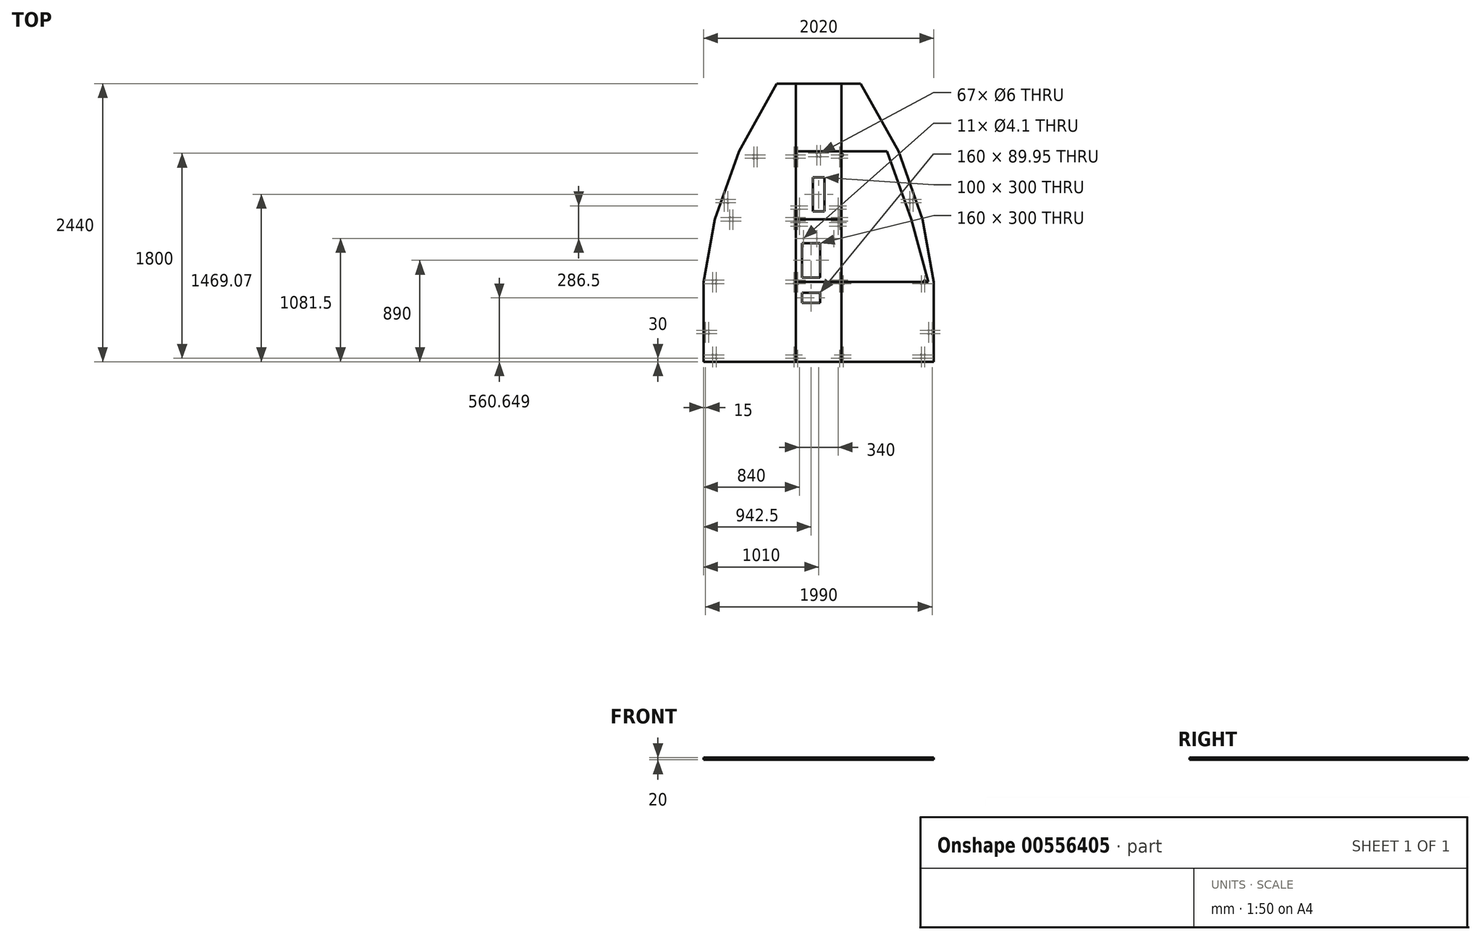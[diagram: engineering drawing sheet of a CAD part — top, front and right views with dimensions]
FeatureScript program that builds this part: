
annotation { "Feature Type Name" : "Feature", "Feature Type Description" : "" }
export const myFeature = defineFeature(function(context is Context, id is Id, definition is map)
    precondition{}
    {
        {
            var Q0;
            Q0=qCreatedBy(makeId("Top.planeOp"),FACE);
            var sketch = newSketch(context, id + "F0", { "sketchPlane" : qUnion([Q0])});
            skLineSegment(sketch, "E0.bottom", {"start": v(200, -350) * mm, "end": v(-200, -350) * mm});
            skLineSegment(sketch, "E0.top", {"start": v(200, 350) * mm, "end": v(-200, 350) * mm});
            skLineSegment(sketch, "E0.left", {"start": v(200, -350) * mm, "end": v(200, 350) * mm});
            skLineSegment(sketch, "E0.right", {"start": v(-200, -350) * mm, "end": v(-200, 350) * mm});
            skPoint(sketch, "E0.middle", {"position": v(0, 0) * mm});
            skCircle(sketch, "E1", {"center": v(185, 335) * mm, "radius": 3 * mm});
            skCircle(sketch, "E2", {"center": v(-185, 335) * mm, "radius": 3 * mm});
            skCircle(sketch, "E3", {"center": v(185, -320) * mm, "radius": 3 * mm});
            skCircle(sketch, "E4", {"center": v(-185, -320) * mm, "radius": 3 * mm});
            skLineSegment(sketch, "E5.bottom", {"start": v(12.5, 165.67) * mm, "end": v(-147.5, 165.67) * mm});
            skLineSegment(sketch, "E5.top", {"start": v(12.5, 255.63) * mm, "end": v(-147.5, 255.63) * mm});
            skLineSegment(sketch, "E5.left", {"start": v(12.5, 165.67) * mm, "end": v(12.5, 255.63) * mm});
            skLineSegment(sketch, "E5.right", {"start": v(-147.5, 165.67) * mm, "end": v(-147.5, 255.63) * mm});
            skPoint(sketch, "E5.middle", {"position": v(-67.5, 210.65) * mm});
            skSolve(sketch);
        }
        {
            var Q0;
            Q0=qSketchRegion(id+"F0",true);
            extrude(context, id + "F1", {"entities" : qUnion([Q0]), "depth" : 20 * mm});
        }
        {
            var Q0;
            Q0=qCreatedBy(makeId("Top.planeOp"),FACE);
            var sketch = newSketch(context, id + "F2", { "sketchPlane" : qUnion([Q0])});
            skLineSegment(sketch, "E6.top", {"start": v(-200, 900) * mm, "end": v(-812, 900) * mm});
            skLineSegment(sketch, "E6.left", {"start": v(-200, 350) * mm, "end": v(-200, 900) * mm});
            skPoint(sketch, "E6.middle", {"position": v(-506, 625) * mm});
            skLineSegment(sketch, "E7", {"start": v(-200, 350) * mm, "end": v(-960, 350) * mm});
            skLineSegment(sketch, "E8", {"start": v(-960, 350) * mm, "end": v(-812, 900) * mm});
            skCircle(sketch, "E9", {"center": v(-215, 885) * mm, "radius": 3 * mm});
            skCircle(sketch, "E10", {"center": v(-215, 365) * mm, "radius": 3 * mm});
            skCircle(sketch, "E11", {"center": v(-930, 365) * mm, "radius": 3 * mm});
            skCircle(sketch, "E12", {"center": v(-782, 885) * mm, "radius": 3 * mm});
            skLineSegment(sketch, "E13.left", {"start": v(-200, 900) * mm, "end": v(-200, 1495) * mm});
            skPoint(sketch, "E13.middle", {"position": v(-506, 1197.5) * mm});
            skLineSegment(sketch, "E14", {"start": v(-200, 1495) * mm, "end": v(-600, 1495) * mm});
            skLineSegment(sketch, "E15", {"start": v(-812, 900) * mm, "end": v(-600, 1495) * mm});
            skCircle(sketch, "E16", {"center": v(-215, 1465) * mm, "radius": 3 * mm});
            skCircle(sketch, "E17", {"center": v(-215, 915) * mm, "radius": 3 * mm});
            skCircle(sketch, "E18", {"center": v(-782, 915) * mm, "radius": 3 * mm});
            skCircle(sketch, "E19", {"center": v(-570, 1465) * mm, "radius": 3 * mm});
            skLineSegment(sketch, "E20", {"start": v(0, 1490.85) * mm, "end": v(0, 501.43) * mm, "construction": true});
            skCircle(sketch, "E21.MirrorC", {"center": v(215, 1465) * mm, "radius": 3 * mm});
            skCircle(sketch, "E22.MirrorC", {"center": v(930, 365) * mm, "radius": 3 * mm});
            skCircle(sketch, "E23.MirrorC", {"center": v(782, 885) * mm, "radius": 3 * mm});
            skCircle(sketch, "E24.MirrorC", {"center": v(782, 915) * mm, "radius": 3 * mm});
            skCircle(sketch, "E25.MirrorC", {"center": v(570, 1465) * mm, "radius": 3 * mm});
            skCircle(sketch, "E26.MirrorC", {"center": v(215, 885) * mm, "radius": 3 * mm});
            skCircle(sketch, "E27.MirrorC", {"center": v(215, 365) * mm, "radius": 3 * mm});
            skCircle(sketch, "E28.MirrorC", {"center": v(215, 915) * mm, "radius": 3 * mm});
            skLineSegment(sketch, "E29.MirrorCS", {"start": v(200, 1495) * mm, "end": v(600, 1495) * mm});
            skLineSegment(sketch, "E30.MirrorCS", {"start": v(960, 350) * mm, "end": v(812, 900) * mm});
            skLineSegment(sketch, "E31.MirrorCS", {"start": v(200, 900) * mm, "end": v(812, 900) * mm});
            skPoint(sketch, "E32.MirrorP", {"position": v(506, 1197.5) * mm});
            skLineSegment(sketch, "E33.MirrorCS", {"start": v(200, 350) * mm, "end": v(200, 900) * mm});
            skPoint(sketch, "E34.MirrorP", {"position": v(506, 625) * mm});
            skLineSegment(sketch, "E35.MirrorCS", {"start": v(200, 350) * mm, "end": v(960, 350) * mm});
            skLineSegment(sketch, "E36.MirrorCS", {"start": v(812, 900) * mm, "end": v(600, 1495) * mm});
            skLineSegment(sketch, "E37.MirrorCS", {"start": v(200, 900) * mm, "end": v(200, 1495) * mm});
            skCircle(sketch, "E38", {"center": v(-900, 365) * mm, "radius": 3 * mm});
            skCircle(sketch, "E39", {"center": v(-752, 885) * mm, "radius": 3 * mm});
            skCircle(sketch, "E40", {"center": v(-752, 915) * mm, "radius": 3 * mm});
            skCircle(sketch, "E41", {"center": v(-570, 1435) * mm, "radius": 3 * mm});
            skCircle(sketch, "E42", {"center": v(-540, 1465) * mm, "radius": 3 * mm});
            skCircle(sketch, "E43", {"center": v(-540, 1435) * mm, "radius": 3 * mm});
            skCircle(sketch, "E44", {"center": v(-215, 1435) * mm, "radius": 3 * mm});
            skCircle(sketch, "E45.MirrorC", {"center": v(215, 1435) * mm, "radius": 3 * mm});
            skCircle(sketch, "E46.MirrorC", {"center": v(540, 1465) * mm, "radius": 3 * mm});
            skCircle(sketch, "E47.MirrorC", {"center": v(540, 1435) * mm, "radius": 3 * mm});
            skCircle(sketch, "E48.MirrorC", {"center": v(570, 1435) * mm, "radius": 3 * mm});
            skCircle(sketch, "E49.MirrorC", {"center": v(752, 915) * mm, "radius": 3 * mm});
            skCircle(sketch, "E50.MirrorC", {"center": v(752, 885) * mm, "radius": 3 * mm});
            skCircle(sketch, "E51.MirrorC", {"center": v(900, 365) * mm, "radius": 3 * mm});
            skSolve(sketch);
        }
        {
            var Q0;
            Q0=makeQuery(id+"F2.imprint","IMPRINT",FACE,{"disambiguationData":[TD([[makeQuery(id+"F2.imprint","IMPRINT",EDGE,{"derivedFrom":sQuery(id+"F2.wireOp",EDGE,"E6.left")}),1.0]])]});
            var Q1;
            Q1=makeQuery(id+"F2.imprint","IMPRINT",FACE,{"disambiguationData":[TD([[makeQuery(id+"F2.imprint","IMPRINT",EDGE,{"derivedFrom":sQuery(id+"F2.wireOp",EDGE,"E22.MirrorC")}),1.0]])]});
            extrude(context, id + "F3", {"entities" : qUnion([Q0, Q1]), "depth" : 20 * mm});
        }
        {
            var Q0;
            Q0=makeQuery(id+"F2.imprint","IMPRINT",FACE,{"disambiguationData":[TD([[makeQuery(id+"F2.imprint","IMPRINT",EDGE,{"derivedFrom":sQuery(id+"F2.wireOp",EDGE,"E6.top")}),-1.0]])]});
            var Q1;
            Q1=makeQuery(id+"F2.imprint","IMPRINT",FACE,{"disambiguationData":[TD([[makeQuery(id+"F2.imprint","IMPRINT",EDGE,{"derivedFrom":sQuery(id+"F2.wireOp",EDGE,"E21.MirrorC")}),1.0]])]});
            extrude(context, id + "F4", {"entities" : qUnion([Q0, Q1]), "depth" : 20 * mm});
        }
        {
            var Q0;
            Q0=qCreatedBy(makeId("Top.planeOp"),FACE);
            var sketch = newSketch(context, id + "F5", { "sketchPlane" : qUnion([Q0])});
            skLineSegment(sketch, "E52.bottom", {"start": v(200, 900) * mm, "end": v(-200, 900) * mm});
            skLineSegment(sketch, "E52.top", {"start": v(200, 350) * mm, "end": v(-200, 350) * mm});
            skLineSegment(sketch, "E52.left", {"start": v(200, 900) * mm, "end": v(200, 350) * mm});
            skLineSegment(sketch, "E52.right", {"start": v(-200, 900) * mm, "end": v(-200, 350) * mm});
            skPoint(sketch, "E52.middle", {"position": v(0, 625) * mm});
            skCircle(sketch, "E53", {"center": v(-132.5, 731.5) * mm, "radius": 2.05 * mm});
            skCircle(sketch, "E54", {"center": v(-17.5, 731.5) * mm, "radius": 2.05 * mm});
            skCircle(sketch, "E55", {"center": v(132.5, 731.5) * mm, "radius": 2.05 * mm});
            skCircle(sketch, "E56", {"center": v(-185, 885) * mm, "radius": 3 * mm});
            skCircle(sketch, "E57", {"center": v(185, 885) * mm, "radius": 3 * mm});
            skCircle(sketch, "E58", {"center": v(-185, 365) * mm, "radius": 3 * mm});
            skCircle(sketch, "E59", {"center": v(185, 365) * mm, "radius": 3 * mm});
            skCircle(sketch, "E60", {"center": v(170, 870) * mm, "radius": 2.05 * mm});
            skCircle(sketch, "E61", {"center": v(170, 840) * mm, "radius": 2.05 * mm});
            skLineSegment(sketch, "E62", {"start": v(0, 625) * mm, "end": v(0, 499.57) * mm, "construction": true});
            skCircle(sketch, "E63.MirrorC", {"center": v(-170, 840) * mm, "radius": 2.05 * mm});
            skCircle(sketch, "E64.MirrorC", {"center": v(-170, 870) * mm, "radius": 2.05 * mm});
            skLineSegment(sketch, "E65.bottom", {"start": v(12.5, 390) * mm, "end": v(-147.5, 390) * mm});
            skLineSegment(sketch, "E65.top", {"start": v(12.5, 690) * mm, "end": v(-147.5, 690) * mm});
            skLineSegment(sketch, "E65.left", {"start": v(12.5, 390) * mm, "end": v(12.5, 690) * mm});
            skLineSegment(sketch, "E65.right", {"start": v(-147.5, 390) * mm, "end": v(-147.5, 690) * mm});
            skPoint(sketch, "E65.middle", {"position": v(-67.5, 540) * mm});
            skSolve(sketch);
        }
        {
            var Q0;
            Q0=qSketchRegion(id+"F5",true);
            extrude(context, id + "F6", {"entities" : qUnion([Q0]), "depth" : 20 * mm});
        }
        {
            var Q0;
            Q0=qCreatedBy(makeId("Top.planeOp"),FACE);
            var sketch = newSketch(context, id + "F7", { "sketchPlane" : qUnion([Q0])});
            skLineSegment(sketch, "E66.bottom", {"start": v(-200, 900) * mm, "end": v(200, 900) * mm});
            skLineSegment(sketch, "E66.top", {"start": v(200, 1495) * mm, "end": v(-200, 1495) * mm});
            skLineSegment(sketch, "E66.left", {"start": v(-200, 900) * mm, "end": v(-200, 1495) * mm});
            skLineSegment(sketch, "E66.right", {"start": v(200, 900) * mm, "end": v(200, 1495) * mm});
            skPoint(sketch, "E66.middle", {"position": v(0, 1197.5) * mm});
            skCircle(sketch, "E67", {"center": v(170, 970) * mm, "radius": 2.05 * mm, "construction": true});
            skCircle(sketch, "E68", {"center": v(170, 940) * mm, "radius": 2.05 * mm, "construction": true});
            skCircle(sketch, "E69", {"center": v(170, 988) * mm, "radius": 2.05 * mm});
            skCircle(sketch, "E70", {"center": v(170, 1018) * mm, "radius": 2.05 * mm});
            skCircle(sketch, "E71.MirrorC", {"center": v(-170, 970) * mm, "radius": 2.05 * mm, "construction": true});
            skCircle(sketch, "E72.MirrorC", {"center": v(-170, 988) * mm, "radius": 2.05 * mm});
            skCircle(sketch, "E73.MirrorC", {"center": v(-170, 1018) * mm, "radius": 2.05 * mm});
            skCircle(sketch, "E74.MirrorC", {"center": v(-170, 940) * mm, "radius": 2.05 * mm, "construction": true});
            skCircle(sketch, "E75", {"center": v(185, 1465) * mm, "radius": 3 * mm});
            skCircle(sketch, "E76", {"center": v(-185, 1465) * mm, "radius": 3 * mm});
            skCircle(sketch, "E77", {"center": v(185, 915) * mm, "radius": 3 * mm});
            skCircle(sketch, "E78", {"center": v(-185, 915) * mm, "radius": 3 * mm});
            skCircle(sketch, "E79", {"center": v(-185, 1435) * mm, "radius": 3 * mm});
            skCircle(sketch, "E80", {"center": v(185, 1435) * mm, "radius": 3 * mm});
            skLineSegment(sketch, "E81.bottom", {"start": v(50, 969.07) * mm, "end": v(-50, 969.07) * mm});
            skLineSegment(sketch, "E81.top", {"start": v(50, 1269.07) * mm, "end": v(-50, 1269.07) * mm});
            skLineSegment(sketch, "E81.left", {"start": v(50, 969.07) * mm, "end": v(50, 1269.07) * mm});
            skLineSegment(sketch, "E81.right", {"start": v(-50, 969.07) * mm, "end": v(-50, 1269.07) * mm});
            skPoint(sketch, "E81.middle", {"position": v(0, 1119.07) * mm});
            skCircle(sketch, "E82", {"center": v(15, 1450) * mm, "radius": 3 * mm});
            skCircle(sketch, "E83", {"center": v(-15, 1450) * mm, "radius": 3 * mm});
            skCircle(sketch, "E84", {"center": v(15, 1480) * mm, "radius": 3 * mm});
            skCircle(sketch, "E85", {"center": v(-15, 1480) * mm, "radius": 3 * mm});
            skSolve(sketch);
        }
        {
            var Q0;
            Q0=qSketchRegion(id+"F7",true);
            extrude(context, id + "F8", {"entities" : qUnion([Q0]), "depth" : 20 * mm});
        }
        {
            var Q0;
            Q0=qCreatedBy(makeId("Top.planeOp"),FACE);
            var sketch = newSketch(context, id + "F9", { "sketchPlane" : qUnion([Q0])});
            skLineSegment(sketch, "E86.bottom", {"start": v(-200, -350) * mm, "end": v(-960, -350) * mm});
            skLineSegment(sketch, "E86.top", {"start": v(-200, 350) * mm, "end": v(-960, 350) * mm});
            skLineSegment(sketch, "E86.left", {"start": v(-200, -350) * mm, "end": v(-200, 350) * mm});
            skLineSegment(sketch, "E86.right", {"start": v(-960, -350) * mm, "end": v(-960, 350) * mm});
            skPoint(sketch, "E86.middle", {"position": v(-580, 0) * mm});
            skPoint(sketch, "E87", {"position": v(-930, 335) * mm});
            skPoint(sketch, "E88", {"position": v(-215, 335) * mm});
            skPoint(sketch, "E89", {"position": v(-930, -320) * mm});
            skPoint(sketch, "E90", {"position": v(-215, -320) * mm});
            skCircle(sketch, "E91", {"center": v(-930, 335) * mm, "radius": 3 * mm});
            skCircle(sketch, "E92", {"center": v(-215, 335) * mm, "radius": 3 * mm});
            skCircle(sketch, "E93", {"center": v(-930, -320) * mm, "radius": 3 * mm});
            skCircle(sketch, "E94", {"center": v(-215, -320) * mm, "radius": 3 * mm});
            skLineSegment(sketch, "E95.bottom", {"start": v(200, -350) * mm, "end": v(960, -350) * mm});
            skLineSegment(sketch, "E95.top", {"start": v(200, 350) * mm, "end": v(960, 350) * mm});
            skLineSegment(sketch, "E95.left", {"start": v(200, -350) * mm, "end": v(200, 350) * mm});
            skLineSegment(sketch, "E95.right", {"start": v(960, -350) * mm, "end": v(960, 350) * mm});
            skPoint(sketch, "E95.middle", {"position": v(580, 0) * mm});
            skCircle(sketch, "E96", {"center": v(215, 335) * mm, "radius": 3 * mm});
            skCircle(sketch, "E97", {"center": v(930, 335) * mm, "radius": 3 * mm});
            skCircle(sketch, "E98", {"center": v(215, -320) * mm, "radius": 3 * mm});
            skCircle(sketch, "E99", {"center": v(930, -320) * mm, "radius": 3 * mm});
            skCircle(sketch, "E100", {"center": v(-930, -290) * mm, "radius": 3 * mm});
            skCircle(sketch, "E101", {"center": v(-900, -320) * mm, "radius": 3 * mm});
            skCircle(sketch, "E102", {"center": v(-900, -290) * mm, "radius": 3 * mm});
            skCircle(sketch, "E103", {"center": v(-215, -290) * mm, "radius": 3 * mm});
            skCircle(sketch, "E104", {"center": v(-900, 335) * mm, "radius": 3 * mm});
            skCircle(sketch, "E105", {"center": v(900, -320) * mm, "radius": 3 * mm});
            skCircle(sketch, "E106", {"center": v(930, -290) * mm, "radius": 3 * mm});
            skCircle(sketch, "E107", {"center": v(900, -290) * mm, "radius": 3 * mm});
            skCircle(sketch, "E108", {"center": v(215, -290) * mm, "radius": 3 * mm});
            skCircle(sketch, "E109", {"center": v(900, 335) * mm, "radius": 3 * mm});
            skSolve(sketch);
        }
        {
            var Q0;
            Q0=qSketchRegion(id+"F9",true);
            extrude(context, id + "F10", {"entities" : qUnion([Q0]), "depth" : 20 * mm});
        }
        {
            var Q0;
            Q0=makeQuery(id+"F8.opExtrude","CAP_FACE",FACE,{"disambiguationData":[OSD([sQuery(id+"F7.wireOp",EDGE,"E66.bottom"),sQuery(id+"F7.wireOp",EDGE,"E66.top"),sQuery(id+"F7.wireOp",EDGE,"E66.left"),sQuery(id+"F7.wireOp",EDGE,"E66.right"),sQuery(id+"F7.wireOp",EDGE,"E69"),sQuery(id+"F7.wireOp",EDGE,"E70"),sQuery(id+"F7.wireOp",EDGE,"E72.MirrorC"),sQuery(id+"F7.wireOp",EDGE,"E73.MirrorC"),sQuery(id+"F7.wireOp",EDGE,"E75"),sQuery(id+"F7.wireOp",EDGE,"E76"),sQuery(id+"F7.wireOp",EDGE,"E77"),sQuery(id+"F7.wireOp",EDGE,"E78"),sQuery(id+"F7.wireOp",EDGE,"E79"),sQuery(id+"F7.wireOp",EDGE,"E80"),sQuery(id+"F7.wireOp",EDGE,"E81.bottom"),sQuery(id+"F7.wireOp",EDGE,"E81.top"),sQuery(id+"F7.wireOp",EDGE,"E81.left"),sQuery(id+"F7.wireOp",EDGE,"E81.right")])],"isStart":false});
            var sketch = newSketch(context, id + "F11", { "sketchPlane" : qUnion([Q0])});
            skLineSegment(sketch, "E110.bottom", {"start": v(-200, 1495) * mm, "end": v(200, 1495) * mm});
            skLineSegment(sketch, "E110.top", {"start": v(-200, 2090) * mm, "end": v(200, 2090) * mm});
            skLineSegment(sketch, "E110.left", {"start": v(-200, 1495) * mm, "end": v(-200, 2090) * mm});
            skLineSegment(sketch, "E110.right", {"start": v(200, 1495) * mm, "end": v(200, 2090) * mm});
            skSolve(sketch);
        }
        {
            var Q0;
            Q0=qSketchRegion(id+"F11",true);
            extrude(context, id + "F12", {"entities" : qUnion([Q0]), "oppositeDirection" : true, "depth" : 20 * mm, "offsetDistance" : 25 * mm});
        }
        {
            var Q0;
            Q0=makeQuery(id+"F8.opExtrude","CAP_FACE",FACE,{"disambiguationData":[OSD([sQuery(id+"F7.wireOp",EDGE,"E66.bottom"),sQuery(id+"F7.wireOp",EDGE,"E66.top"),sQuery(id+"F7.wireOp",EDGE,"E66.left"),sQuery(id+"F7.wireOp",EDGE,"E66.right"),sQuery(id+"F7.wireOp",EDGE,"E69"),sQuery(id+"F7.wireOp",EDGE,"E70"),sQuery(id+"F7.wireOp",EDGE,"E72.MirrorC"),sQuery(id+"F7.wireOp",EDGE,"E73.MirrorC"),sQuery(id+"F7.wireOp",EDGE,"E75"),sQuery(id+"F7.wireOp",EDGE,"E76"),sQuery(id+"F7.wireOp",EDGE,"E77"),sQuery(id+"F7.wireOp",EDGE,"E78"),sQuery(id+"F7.wireOp",EDGE,"E79"),sQuery(id+"F7.wireOp",EDGE,"E80"),sQuery(id+"F7.wireOp",EDGE,"E81.bottom"),sQuery(id+"F7.wireOp",EDGE,"E81.top"),sQuery(id+"F7.wireOp",EDGE,"E81.left"),sQuery(id+"F7.wireOp",EDGE,"E81.right")])],"isStart":false});
            var sketch = newSketch(context, id + "F13", { "sketchPlane" : qUnion([Q0])});
            skLineSegment(sketch, "E111", {"start": v(-200, 1495) * mm, "end": v(-600, 1495) * mm});
            skLineSegment(sketch, "E112", {"start": v(-600, 1495) * mm, "end": v(-268, 2090) * mm});
            skLineSegment(sketch, "E113", {"start": v(-268, 2090) * mm, "end": v(-200, 2090) * mm});
            skLineSegment(sketch, "E114", {"start": v(-200, 2090) * mm, "end": v(-200, 1495) * mm});
            skSolve(sketch);
        }
        {
            var Q0;
            Q0=makeQuery(id+"F13.imprint","IMPRINT",FACE,{"disambiguationData":[TD([[makeQuery(id+"F13.imprint","IMPRINT",EDGE,{"derivedFrom":sQuery(id+"F13.wireOp",EDGE,"E111")}),-1.0]])]});
            extrude(context, id + "F14", {"entities" : qUnion([Q0]), "oppositeDirection" : true, "depth" : 20 * mm, "offsetDistance" : 25 * mm});
        }
        {
            var Q0;
            Q0=makeQuery(id+"F8.opExtrude","CAP_FACE",FACE,{"disambiguationData":[OSD([sQuery(id+"F7.wireOp",EDGE,"E66.bottom"),sQuery(id+"F7.wireOp",EDGE,"E66.top"),sQuery(id+"F7.wireOp",EDGE,"E66.left"),sQuery(id+"F7.wireOp",EDGE,"E66.right"),sQuery(id+"F7.wireOp",EDGE,"E69"),sQuery(id+"F7.wireOp",EDGE,"E70"),sQuery(id+"F7.wireOp",EDGE,"E72.MirrorC"),sQuery(id+"F7.wireOp",EDGE,"E73.MirrorC"),sQuery(id+"F7.wireOp",EDGE,"E75"),sQuery(id+"F7.wireOp",EDGE,"E76"),sQuery(id+"F7.wireOp",EDGE,"E77"),sQuery(id+"F7.wireOp",EDGE,"E78"),sQuery(id+"F7.wireOp",EDGE,"E79"),sQuery(id+"F7.wireOp",EDGE,"E80"),sQuery(id+"F7.wireOp",EDGE,"E81.bottom"),sQuery(id+"F7.wireOp",EDGE,"E81.top"),sQuery(id+"F7.wireOp",EDGE,"E81.left"),sQuery(id+"F7.wireOp",EDGE,"E81.right")])],"isStart":false});
            var sketch = newSketch(context, id + "F15", { "sketchPlane" : qUnion([Q0])});
            skLineSegment(sketch, "E115", {"start": v(200, 1495) * mm, "end": v(600, 1495) * mm});
            skLineSegment(sketch, "E116", {"start": v(600, 1495) * mm, "end": v(268, 2090) * mm});
            skLineSegment(sketch, "E117", {"start": v(268, 2090) * mm, "end": v(200, 2090) * mm});
            skLineSegment(sketch, "E118", {"start": v(200, 2090) * mm, "end": v(200, 1495) * mm});
            skSolve(sketch);
        }
        {
            var Q0;
            Q0=qSketchRegion(id+"F15",true);
            extrude(context, id + "F16", {"entities" : qUnion([Q0]), "oppositeDirection" : true, "depth" : 20 * mm, "offsetDistance" : 25 * mm});
        }
        {
            var Q0;
            Q0=makeQuery(id+"F10.opExtrude","CAP_FACE",FACE,{"disambiguationData":[OSD([sQuery(id+"F9.wireOp",EDGE,"E86.bottom"),sQuery(id+"F9.wireOp",EDGE,"E86.top"),sQuery(id+"F9.wireOp",EDGE,"E86.left"),sQuery(id+"F9.wireOp",EDGE,"E86.right"),sQuery(id+"F9.wireOp",EDGE,"E91"),sQuery(id+"F9.wireOp",EDGE,"E92"),sQuery(id+"F9.wireOp",EDGE,"E93"),sQuery(id+"F9.wireOp",EDGE,"E94"),sQuery(id+"F9.wireOp",EDGE,"E100"),sQuery(id+"F9.wireOp",EDGE,"E101"),sQuery(id+"F9.wireOp",EDGE,"E102"),sQuery(id+"F9.wireOp",EDGE,"E103"),sQuery(id+"F9.wireOp",EDGE,"E104")])],"isStart":true});
            var sketch = newSketch(context, id + "F17", { "sketchPlane" : qUnion([Q0])});
            skLineSegment(sketch, "E119.bottom", {"start": v(-960, -350) * mm, "end": v(-1010, -350) * mm});
            skLineSegment(sketch, "E119.top", {"start": v(-960, 350) * mm, "end": v(-1010, 350) * mm});
            skLineSegment(sketch, "E119.left", {"start": v(-960, -350) * mm, "end": v(-960, 350) * mm});
            skLineSegment(sketch, "E119.right", {"start": v(-1010, -350) * mm, "end": v(-1010, 350) * mm});
            skCircle(sketch, "E120", {"center": v(-965, 75) * mm, "radius": 3 * mm});
            skCircle(sketch, "E121", {"center": v(-995, 75) * mm, "radius": 3 * mm});
            skCircle(sketch, "E122", {"center": v(-965, 105) * mm, "radius": 3 * mm});
            skCircle(sketch, "E123", {"center": v(-995, 105) * mm, "radius": 3 * mm});
            skSolve(sketch);
        }
        {
            var Q0;
            Q0=makeQuery(id+"F10.opExtrude","CAP_FACE",FACE,{"disambiguationData":[OSD([sQuery(id+"F9.wireOp",EDGE,"E95.bottom"),sQuery(id+"F9.wireOp",EDGE,"E95.top"),sQuery(id+"F9.wireOp",EDGE,"E95.left"),sQuery(id+"F9.wireOp",EDGE,"E95.right"),sQuery(id+"F9.wireOp",EDGE,"E96"),sQuery(id+"F9.wireOp",EDGE,"E97"),sQuery(id+"F9.wireOp",EDGE,"E98"),sQuery(id+"F9.wireOp",EDGE,"E99"),sQuery(id+"F9.wireOp",EDGE,"E105"),sQuery(id+"F9.wireOp",EDGE,"E106"),sQuery(id+"F9.wireOp",EDGE,"E107"),sQuery(id+"F9.wireOp",EDGE,"E108"),sQuery(id+"F9.wireOp",EDGE,"E109")])],"isStart":true});
            var sketch = newSketch(context, id + "F18", { "sketchPlane" : qUnion([Q0])});
            skLineSegment(sketch, "E124.bottom", {"start": v(960, 350) * mm, "end": v(1010, 350) * mm});
            skLineSegment(sketch, "E124.top", {"start": v(960, -350) * mm, "end": v(1010, -350) * mm});
            skLineSegment(sketch, "E124.left", {"start": v(960, 350) * mm, "end": v(960, -350) * mm});
            skLineSegment(sketch, "E124.right", {"start": v(1010, 350) * mm, "end": v(1010, -350) * mm});
            skCircle(sketch, "E125", {"center": v(995, 75) * mm, "radius": 3 * mm});
            skCircle(sketch, "E126", {"center": v(965, 75) * mm, "radius": 3 * mm});
            skCircle(sketch, "E127", {"center": v(995, 105) * mm, "radius": 3 * mm});
            skCircle(sketch, "E128", {"center": v(965, 105) * mm, "radius": 3 * mm});
            skSolve(sketch);
        }
        {
            var Q0;
            Q0=qSketchRegion(id+"F17",true);
            extrude(context, id + "F19", {"entities" : qUnion([Q0]), "operationType" : NewBodyOperationType.ADD, "oppositeDirection" : true, "depth" : 20 * mm, "offsetDistance" : 25 * mm});
        }
        {
            var Q0;
            Q0=qSketchRegion(id+"F18",true);
            extrude(context, id + "F20", {"entities" : qUnion([Q0]), "operationType" : NewBodyOperationType.ADD, "oppositeDirection" : true, "depth" : 20 * mm, "offsetDistance" : 25 * mm});
        }
        {
            var Q0;
            Q0=makeQuery(id+"F4.opExtrude","CAP_FACE",FACE,{"disambiguationData":[OSD([sQuery(id+"F2.wireOp",EDGE,"E6.top"),sQuery(id+"F2.wireOp",EDGE,"E13.left"),sQuery(id+"F2.wireOp",EDGE,"E14"),sQuery(id+"F2.wireOp",EDGE,"E15"),sQuery(id+"F2.wireOp",EDGE,"E16"),sQuery(id+"F2.wireOp",EDGE,"E17"),sQuery(id+"F2.wireOp",EDGE,"E18"),sQuery(id+"F2.wireOp",EDGE,"E19"),sQuery(id+"F2.wireOp",EDGE,"E40"),sQuery(id+"F2.wireOp",EDGE,"E41"),sQuery(id+"F2.wireOp",EDGE,"E42"),sQuery(id+"F2.wireOp",EDGE,"E43"),sQuery(id+"F2.wireOp",EDGE,"E44")])],"isStart":true});
            var sketch = newSketch(context, id + "F21", { "sketchPlane" : qUnion([Q0])});
            skLineSegment(sketch, "E129", {"start": v(-600, -1495) * mm, "end": v(-812, -900) * mm});
            skLineSegment(sketch, "E130", {"start": v(-812, -900) * mm, "end": v(-912, -900) * mm});
            skLineSegment(sketch, "E131", {"start": v(-912, -900) * mm, "end": v(-700, -1495) * mm});
            skLineSegment(sketch, "E132", {"start": v(-700, -1495) * mm, "end": v(-600, -1495) * mm});
            skCircle(sketch, "E133", {"center": v(-798.5, -1075) * mm, "radius": 3 * mm});
            skCircle(sketch, "E134", {"center": v(-828.5, -1075) * mm, "radius": 3 * mm});
            skCircle(sketch, "E135", {"center": v(-798.5, -1045) * mm, "radius": 3 * mm});
            skCircle(sketch, "E136", {"center": v(-828.5, -1045) * mm, "radius": 3 * mm});
            skSolve(sketch);
        }
        {
            var Q0;
            Q0=makeQuery(id+"F4.opExtrude","CAP_FACE",FACE,{"disambiguationData":[OSD([sQuery(id+"F2.wireOp",EDGE,"E21.MirrorC"),sQuery(id+"F2.wireOp",EDGE,"E24.MirrorC"),sQuery(id+"F2.wireOp",EDGE,"E25.MirrorC"),sQuery(id+"F2.wireOp",EDGE,"E28.MirrorC"),sQuery(id+"F2.wireOp",EDGE,"E29.MirrorCS"),sQuery(id+"F2.wireOp",EDGE,"E31.MirrorCS"),sQuery(id+"F2.wireOp",EDGE,"E36.MirrorCS"),sQuery(id+"F2.wireOp",EDGE,"E37.MirrorCS"),sQuery(id+"F2.wireOp",EDGE,"E45.MirrorC"),sQuery(id+"F2.wireOp",EDGE,"E46.MirrorC"),sQuery(id+"F2.wireOp",EDGE,"E47.MirrorC"),sQuery(id+"F2.wireOp",EDGE,"E48.MirrorC"),sQuery(id+"F2.wireOp",EDGE,"E49.MirrorC")])],"isStart":true});
            var sketch = newSketch(context, id + "F22", { "sketchPlane" : qUnion([Q0])});
            skLineSegment(sketch, "E137", {"start": v(812, -900) * mm, "end": v(600, -1495) * mm});
            skLineSegment(sketch, "E138", {"start": v(600, -1495) * mm, "end": v(700, -1495) * mm});
            skLineSegment(sketch, "E139", {"start": v(700, -1495) * mm, "end": v(912, -900) * mm});
            skLineSegment(sketch, "E140", {"start": v(912, -900) * mm, "end": v(812, -900) * mm});
            skCircle(sketch, "E141", {"center": v(828.42, -1075) * mm, "radius": 3 * mm});
            skCircle(sketch, "E142", {"center": v(798.42, -1075) * mm, "radius": 3 * mm});
            skCircle(sketch, "E143", {"center": v(828.42, -1045) * mm, "radius": 3 * mm});
            skCircle(sketch, "E144", {"center": v(798.42, -1045) * mm, "radius": 3 * mm});
            skSolve(sketch);
        }
        {
            var Q0;
            Q0=qSketchRegion(id+"F21",true);
            extrude(context, id + "F23", {"entities" : qUnion([Q0]), "operationType" : NewBodyOperationType.ADD, "oppositeDirection" : true, "depth" : 20 * mm, "offsetDistance" : 25 * mm});
        }
        {
            var Q0;
            Q0=qSketchRegion(id+"F22",true);
            extrude(context, id + "F24", {"entities" : qUnion([Q0]), "operationType" : NewBodyOperationType.ADD, "oppositeDirection" : true, "depth" : 20 * mm, "offsetDistance" : 25 * mm});
        }
        {
            var Q0;
            Q0=makeQuery(id+"F3.opExtrude","CAP_FACE",FACE,{"disambiguationData":[OSD([sQuery(id+"F2.wireOp",EDGE,"E6.left"),sQuery(id+"F2.wireOp",EDGE,"E7"),sQuery(id+"F2.wireOp",EDGE,"E8"),sQuery(id+"F2.wireOp",EDGE,"E9"),sQuery(id+"F2.wireOp",EDGE,"E10"),sQuery(id+"F2.wireOp",EDGE,"E11"),sQuery(id+"F2.wireOp",EDGE,"E12"),sQuery(id+"F2.wireOp",EDGE,"E6.top"),sQuery(id+"F2.wireOp",EDGE,"E38"),sQuery(id+"F2.wireOp",EDGE,"E39")])],"isStart":true});
            var sketch = newSketch(context, id + "F25", { "sketchPlane" : qUnion([Q0])});
            skLineSegment(sketch, "E145", {"start": v(-812, -900) * mm, "end": v(-912, -900) * mm});
            skLineSegment(sketch, "E146", {"start": v(-912, -900) * mm, "end": v(-1010, -350) * mm});
            skLineSegment(sketch, "E147", {"start": v(-1010, -350) * mm, "end": v(-960, -350) * mm});
            skLineSegment(sketch, "E148", {"start": v(-960, -350) * mm, "end": v(-812, -900) * mm});
            skSolve(sketch);
        }
        {
            var Q0;
            Q0=qSketchRegion(id+"F25",true);
            extrude(context, id + "F26", {"entities" : qUnion([Q0]), "operationType" : NewBodyOperationType.ADD, "oppositeDirection" : true, "depth" : 20 * mm, "offsetDistance" : 25 * mm});
        }
        {
            var Q0;
            Q0=makeQuery(id+"F3.opExtrude","CAP_FACE",FACE,{"disambiguationData":[OSD([sQuery(id+"F2.wireOp",EDGE,"E22.MirrorC"),sQuery(id+"F2.wireOp",EDGE,"E23.MirrorC"),sQuery(id+"F2.wireOp",EDGE,"E26.MirrorC"),sQuery(id+"F2.wireOp",EDGE,"E27.MirrorC"),sQuery(id+"F2.wireOp",EDGE,"E30.MirrorCS"),sQuery(id+"F2.wireOp",EDGE,"E33.MirrorCS"),sQuery(id+"F2.wireOp",EDGE,"E31.MirrorCS"),sQuery(id+"F2.wireOp",EDGE,"E35.MirrorCS"),sQuery(id+"F2.wireOp",EDGE,"E50.MirrorC"),sQuery(id+"F2.wireOp",EDGE,"E51.MirrorC")])],"isStart":true});
            var sketch = newSketch(context, id + "F27", { "sketchPlane" : qUnion([Q0])});
            skLineSegment(sketch, "E149", {"start": v(960, -350) * mm, "end": v(812, -900) * mm});
            skLineSegment(sketch, "E150", {"start": v(812, -900) * mm, "end": v(912, -900) * mm});
            skLineSegment(sketch, "E151", {"start": v(912, -900) * mm, "end": v(1010, -350) * mm});
            skLineSegment(sketch, "E152", {"start": v(1010, -350) * mm, "end": v(960, -350) * mm});
            skSolve(sketch);
        }
        {
            var Q0;
            Q0=qSketchRegion(id+"F27",true);
            extrude(context, id + "F28", {"entities" : qUnion([Q0]), "operationType" : NewBodyOperationType.ADD, "oppositeDirection" : true, "depth" : 20 * mm, "offsetDistance" : 25 * mm});
        }
        {
            var Q0;
            Q0=makeQuery(id+"F16.opExtrude","CAP_FACE",FACE,{"disambiguationData":[OSD([sQuery(id+"F15.wireOp",EDGE,"E115"),sQuery(id+"F15.wireOp",EDGE,"E116"),sQuery(id+"F15.wireOp",EDGE,"E117"),sQuery(id+"F15.wireOp",EDGE,"E118")])],"isStart":false});
            var sketch = newSketch(context, id + "F29", { "sketchPlane" : qUnion([Q0])});
            skLineSegment(sketch, "E153", {"start": v(600, -1495) * mm, "end": v(268, -2090) * mm});
            skLineSegment(sketch, "E154", {"start": v(268, -2090) * mm, "end": v(368, -2090) * mm});
            skLineSegment(sketch, "E155", {"start": v(368, -2090) * mm, "end": v(700, -1495) * mm});
            skLineSegment(sketch, "E156", {"start": v(700, -1495) * mm, "end": v(600, -1495) * mm});
            skSolve(sketch);
        }
        {
            var Q0;
            Q0=qSketchRegion(id+"F29",true);
            extrude(context, id + "F30", {"entities" : qUnion([Q0]), "operationType" : NewBodyOperationType.ADD, "oppositeDirection" : true, "depth" : 20 * mm, "offsetDistance" : 25 * mm});
        }
        {
            var Q0;
            Q0=makeQuery(id+"F14.opExtrude","CAP_FACE",FACE,{"disambiguationData":[OSD([sQuery(id+"F13.wireOp",EDGE,"E111"),sQuery(id+"F13.wireOp",EDGE,"E112"),sQuery(id+"F13.wireOp",EDGE,"E113"),sQuery(id+"F13.wireOp",EDGE,"E114")])],"isStart":false});
            var sketch = newSketch(context, id + "F31", { "sketchPlane" : qUnion([Q0])});
            skLineSegment(sketch, "E157", {"start": v(-600, -1495) * mm, "end": v(-268, -2090) * mm});
            skLineSegment(sketch, "E158", {"start": v(-268, -2090) * mm, "end": v(-368, -2090) * mm});
            skLineSegment(sketch, "E159", {"start": v(-368, -2090) * mm, "end": v(-700, -1495) * mm});
            skLineSegment(sketch, "E160", {"start": v(-700, -1495) * mm, "end": v(-600, -1495) * mm});
            skSolve(sketch);
        }
        {
            var Q0;
            Q0=qSketchRegion(id+"F31",true);
            extrude(context, id + "F32", {"entities" : qUnion([Q0]), "operationType" : NewBodyOperationType.ADD, "oppositeDirection" : true, "depth" : 20 * mm, "offsetDistance" : 25 * mm});
        }
    });
